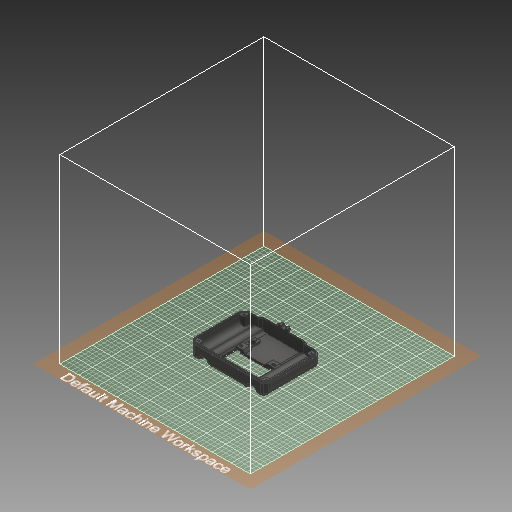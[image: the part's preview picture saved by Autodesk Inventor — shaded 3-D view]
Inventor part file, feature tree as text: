
AUTODESK INVENTOR PART (.ipt)
format: ipt  version: 2019.4 (Build 234330000, 330)  size: 1,577,472 bytes
history: native  units: in
note: dims shown in document units (in); Inventor stores cm internally (conversion verified against a paired STEP export)
features: sketch x17, extrude x13, fillet x8, chamfer x3, move_body x3, direct_edit x2, imported_body x1
ambient origin geometry x8: Origin, YZ Plane, XZ Plane, XY Plane, X Axis, Y Axis, Z Axis, Center Point
bodies: Solid1 (feature_tree)
feature tree (47):
  imported_body  "Base1"
  fillet  "Fillet1"  Radius=0.3937in
  fillet  "Fillet2"  Radius=0.5512in
  fillet  "Fillet3"  Radius=0.1969in
  fillet  "Fillet4"  Radius=0.1969in
  fillet  "Fillet5"  Radius=0.1969in
  sketch  "Sketch1"  dims[d5=0.5906in d6=1.6142in]
  extrude  "Extrusion1"  Depth=1.6142in
  extrude  "Extrusion2"  Depth=1.7717in
  extrude  "Extrusion3"  Depth=0.2362in
  chamfer  "Chamfer1"  Distance=1.6437in
  extrude  "Extrusion4"  Depth=0.5906in
  extrude  "Extrusion5"  Depth=0.5906in
  sketch  "Sketch7"  dims[d16=0.126in d17=1.6437in d18=0.0in]
  chamfer  "Chamfer2"  Distance=0.1969in
  extrude  "Extrusion8"  Depth=0.1969in
  fillet  "Fillet7"  Radius=0.122in
  extrude  "Extrusion9"  Depth=0.0945in TaperAngle=0.0deg
  extrude  "Extrusion10"  Depth=0.3937in
  fillet  "Fillet8"  Radius=0.3937in
  extrude  "Extrusion11"  Depth=0.1969in
  sketch  "Sketch14"  dims[d25=0.5906in]
  extrude  "Extrusion12"  Depth=0.3937in
  extrude  "Extrusion13"  Depth=0.3937in
  extrude  "Extrusion14"  Depth=0.3937in
  direct_edit  "Direct Edit1"
  sketch  "Sketch18"  dims[d37=0.3937in d38=0.3937in d39=0.3937in]
  extrude  "Extrusion15"  Depth=0.1575in TaperAngle=0.0deg
  fillet  "Fillet9"  Radius=0.1378in
  chamfer  "Chamfer3"  Distance=0.1575in
  direct_edit  "Direct Edit2"
  sketch  "Sketch2"  dims[d7=3.2283in d8=1.7717in]
  sketch  "Sketch3"  dims[d9=1.6437in d10=0.0in d12=0.2362in]
  sketch  "Sketch4"  dims[d13=0.2362in]
  sketch  "Sketch5"  dims[d14=0.126in]
  sketch  "Sketch6"  dims[d15=0.126in]
  sketch  "Sketch10"  dims[d19=0.5906in d20=0.5906in]
  sketch  "Sketch11"  dims[d21=0.5906in d22=0.5906in]
  sketch  "Sketch12"  dims[d23=0.2953in]
  sketch  "Sketch13"  dims[d24=0.3937in]
  sketch  "Sketch15"  dims[d26=0.3937in d27=0.1969in d28=0.0in]
  sketch  "Sketch16"  dims[d29=0.1969in d30=0.0787in d31=45.0deg d32=0.122in d33=0.122in]
  sketch  "Sketch17"  dims[d34=0.122in d35=0.0945in d36=0.0in]
  sketch  "Sketch19"  dims[d40=0.3937in d41=0.1969in d42=0.3937in d43=0.3937in d44=0.3937in d45=0.1575in d46=0.0in d47=0.1378in d48=0.0787in d49=45.0deg d61=0.1575in d62=0.0in d63=0.3937in d64=0.3543in d65=0.4528in d68=0.1575in d69=0.0in d70=0.2362in d71=0.2362in d72=0.0787in d73=0.0787in d74=0.1378in d75=0.0in d76=0.1772in d77=0.3051in d78=0.6102in d79=0.0591in d80=0.0591in d81=0.1969in d82=0.0in d83=0.1969in d84=0.1969in d85=0.1969in d86=0.0in d87=0.2362in d88=0.1575in d89=0.1575in d90=0.1575in d91=0.1575in d92=1.4469in d93=0.0in d94=0.315in d95=0.315in d96=0.315in d97=0.315in d98=0.315in d99=0.0in d100=0.7087in d101=0.0in d102=0.0in d103=0.0in d104=0.0394in d105=0.0in d106=0.0in d107=0.0394in d109=0.0039in d110=0.0039in d111=0.3622in d112=0.4606in d113=0.3937in d114=0.0in d115=0.1772in d116=0.1181in d117=0.0787in d118=45.0deg d119=0.0in d120=-0.0079in d121=0.0in]
  move_body  "Move1"
  move_body  "Move2"
  move_body  "Move3"
